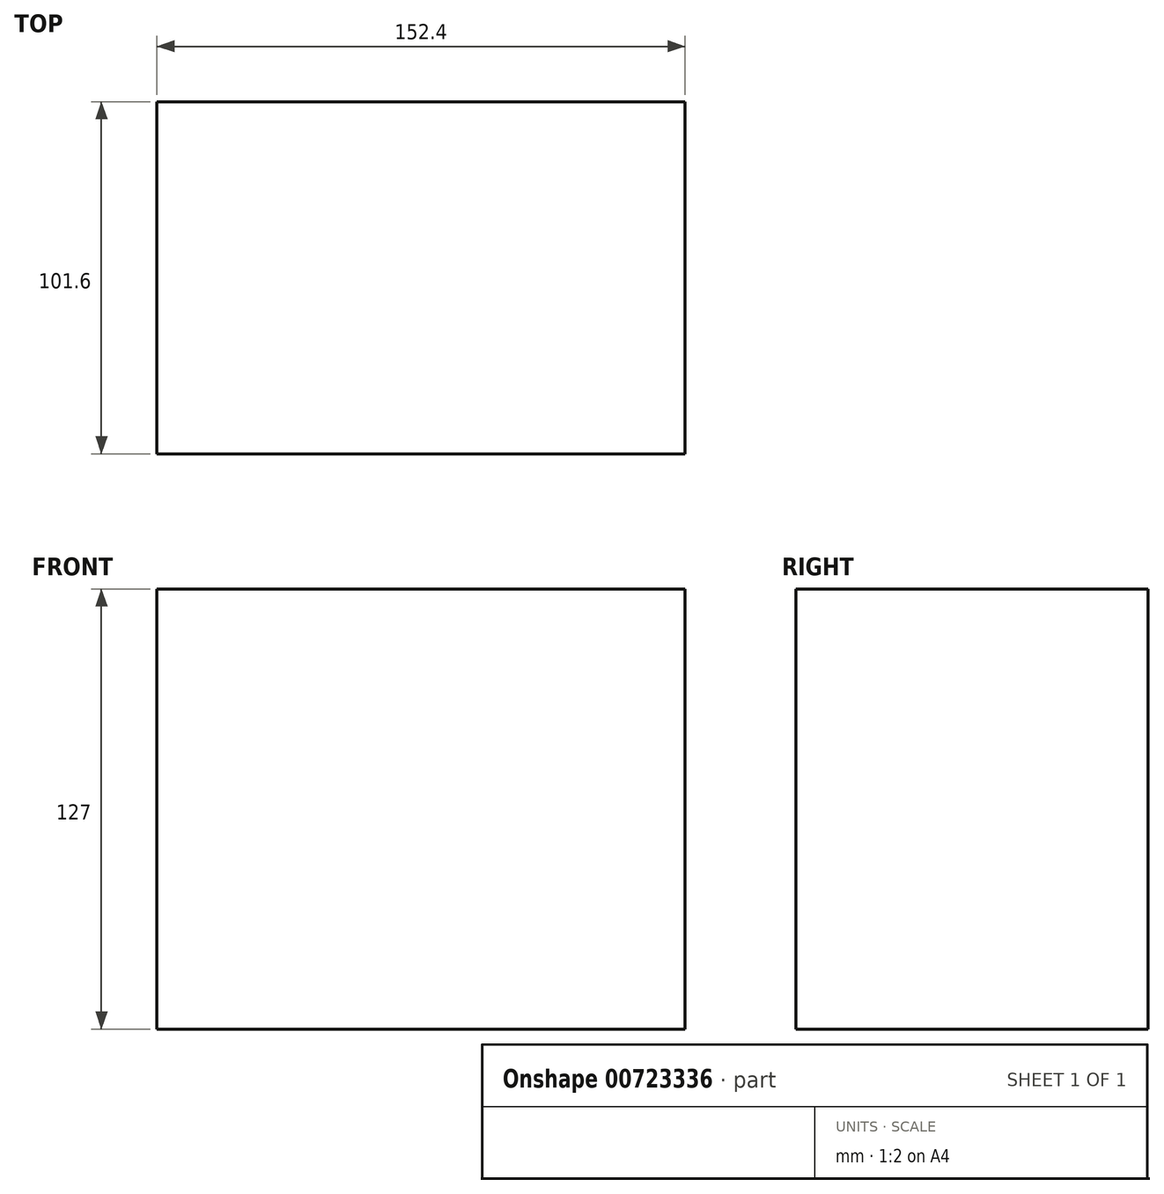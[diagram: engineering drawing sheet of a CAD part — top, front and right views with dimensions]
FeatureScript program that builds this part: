
annotation { "Feature Type Name" : "Feature", "Feature Type Description" : "" }
export const myFeature = defineFeature(function(context is Context, id is Id, definition is map)
    precondition{}
    {
        {
            var Q0;
            Q0=qCreatedBy(makeId("Front.planeOp"),FACE);
            var sketch = newSketch(context, id + "F0", { "sketchPlane" : qUnion([Q0])});
            skLineSegment(sketch, "E0", {"start": v(-74.8, -76.58) * mm, "end": v(77.6, -76.58) * mm});
            skLineSegment(sketch, "E1", {"start": v(-74.8, -76.58) * mm, "end": v(-74.8, 50.42) * mm});
            skLineSegment(sketch, "E2", {"start": v(77.6, -76.58) * mm, "end": v(77.6, 50.42) * mm});
            skLineSegment(sketch, "E3", {"start": v(-74.8, 50.42) * mm, "end": v(77.6, 50.42) * mm});
            skSolve(sketch);
        }
        {
            var Q0;
            Q0 = qSketchRegion(id + "F0", true);
            extrude(context, id + "F1", {"entities" : qUnion([Q0]), "depth" : 101.6 * mm, "offsetDistance" : 25.4 * mm});
        }
    });
